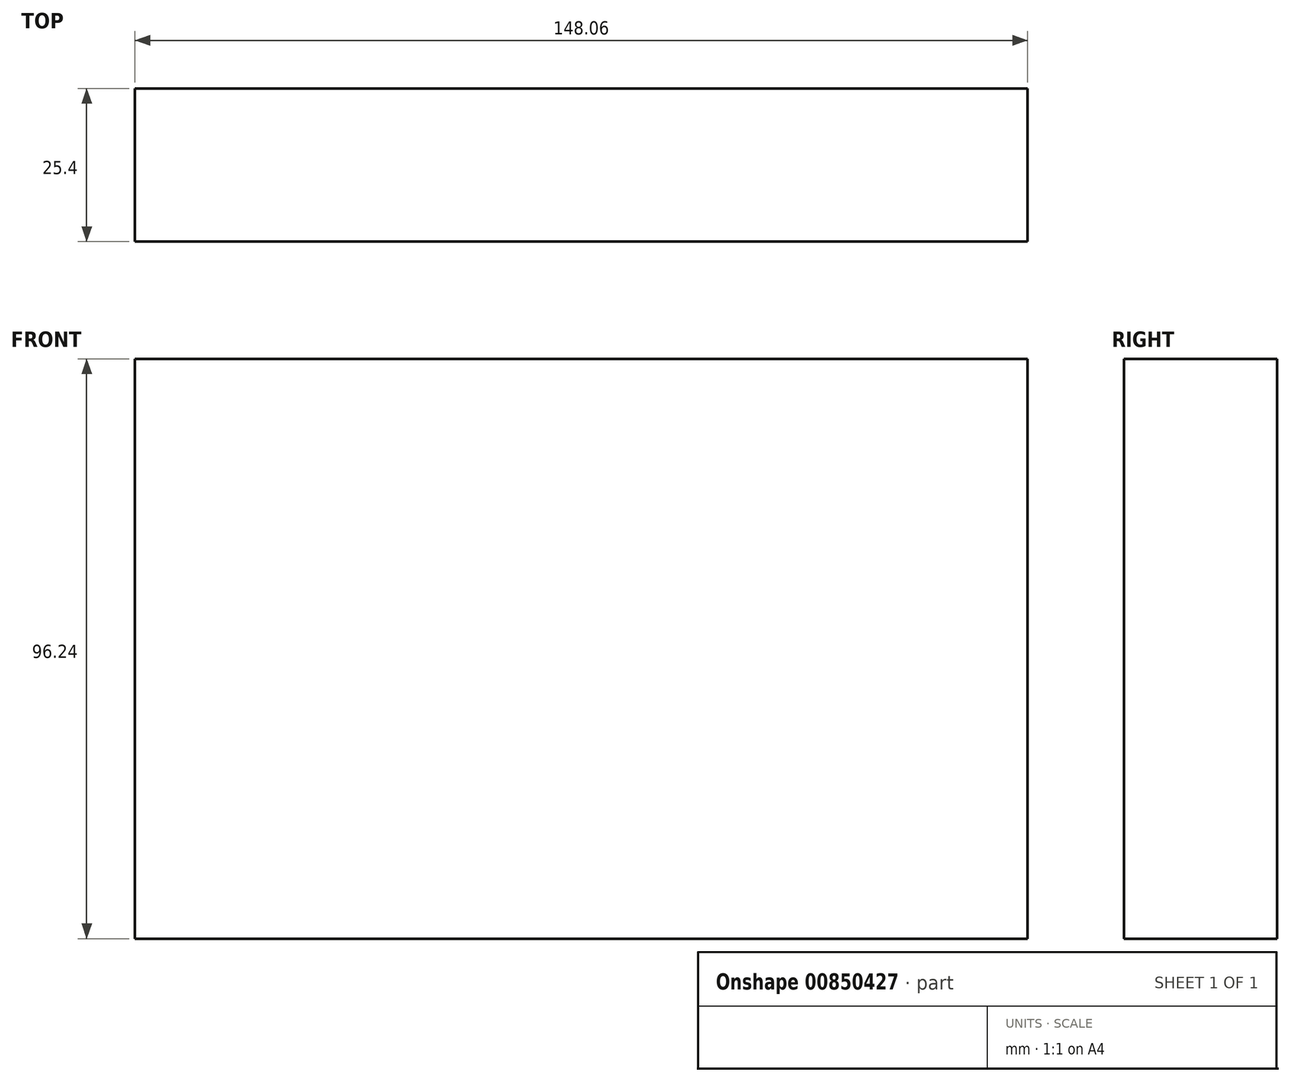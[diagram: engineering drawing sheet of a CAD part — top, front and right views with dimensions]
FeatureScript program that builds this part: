
annotation { "Feature Type Name" : "Feature", "Feature Type Description" : "" }
export const myFeature = defineFeature(function(context is Context, id is Id, definition is map)
    precondition{}
    {
        {
            var Q0;
            Q0=qCreatedBy(makeId("Front.planeOp"),FACE);
            var sketch = newSketch(context, id + "F0", { "sketchPlane" : qUnion([Q0])});
            skLineSegment(sketch, "E0.bottom", {"start": v(-236.52, 4.03) * mm, "end": v(-88.46, 4.03) * mm});
            skLineSegment(sketch, "E0.top", {"start": v(-236.52, -92.2) * mm, "end": v(-88.46, -92.2) * mm});
            skLineSegment(sketch, "E0.left", {"start": v(-236.52, 4.03) * mm, "end": v(-236.52, -92.2) * mm});
            skLineSegment(sketch, "E0.right", {"start": v(-88.46, 4.03) * mm, "end": v(-88.46, -92.2) * mm});
            skSolve(sketch);
        }
        {
            var Q0;
            Q0 = qSketchRegion(id + "F0", true);
            extrude(context, id + "F1", {"entities" : qUnion([Q0]), "depth" : 25.4 * mm, "offsetDistance" : 25.4 * mm});
        }
    });
